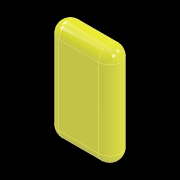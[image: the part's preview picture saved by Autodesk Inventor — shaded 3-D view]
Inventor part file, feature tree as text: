
AUTODESK INVENTOR PART (.ipt)
format: ipt  version: 2020 (Build 240168000, 168)  size: 120,832 bytes
history: native  units: mm
features: fillet x2, other x1, extrude x1, plane x1, sketch x1
ambient origin geometry x8: Origin, YZ Plane, XZ Plane, XY Plane, X Axis, Y Axis, Z Axis, Center Point
bodies: Body1 (feature_tree)
feature tree (6):
  other  "實體1"
  extrude  "擠出1"  Depth=110.0mm
  fillet  "圓角1"  Radius=180.0mm
  fillet  "圓角2"  Radius=40.0mm
  plane  "工作平面1"
  sketch  "草圖1"
